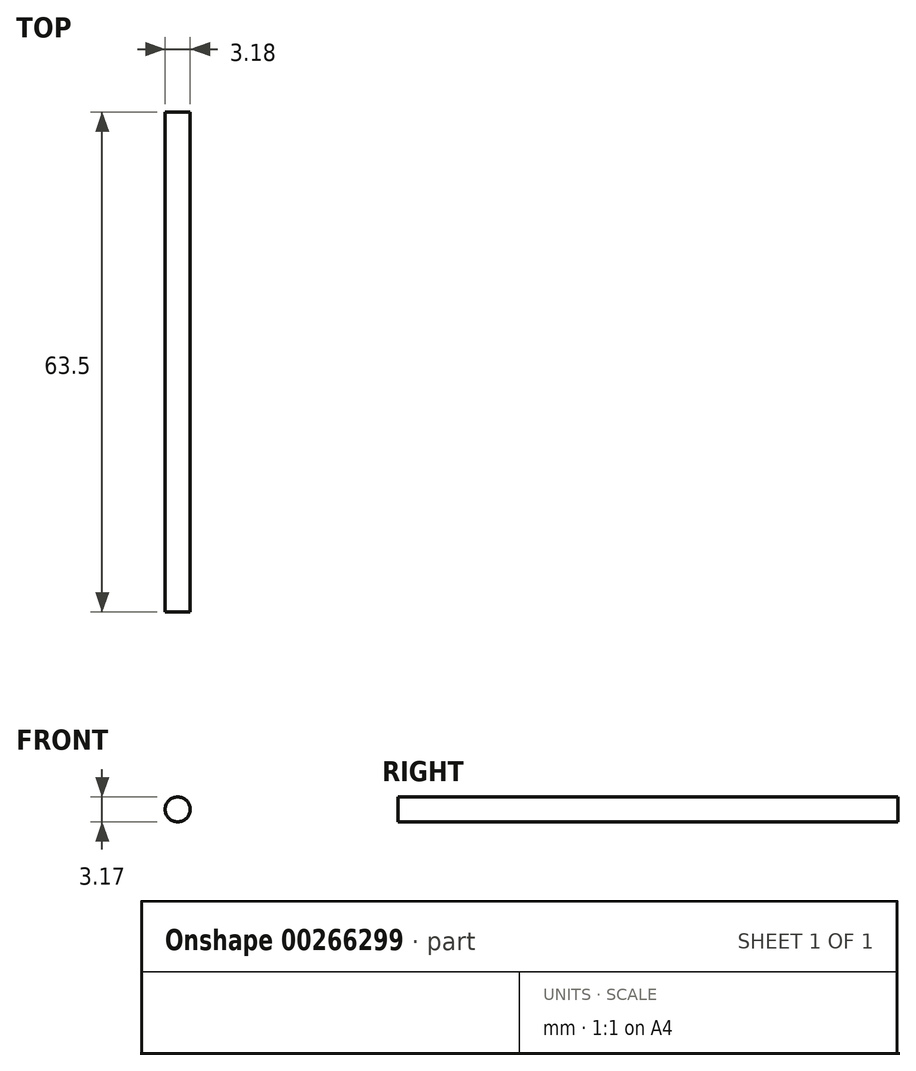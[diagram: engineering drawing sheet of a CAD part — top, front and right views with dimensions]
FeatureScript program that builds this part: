
annotation { "Feature Type Name" : "Feature", "Feature Type Description" : "" }
export const myFeature = defineFeature(function(context is Context, id is Id, definition is map)
    precondition{}
    {
        {
            var Q0;
            Q0=qCreatedBy(makeId("Front.planeOp"),FACE);
            var sketch = newSketch(context, id + "F0", { "sketchPlane" : qUnion([Q0])});
            skCircle(sketch, "E0", {"center": v(-39.23, 40.44) * mm, "radius": 1.59 * mm});
            skSolve(sketch);
        }
        {
            var Q0;
            Q0=makeQuery(id+"F0.imprint","IMPRINT",FACE,{"disambiguationData":[TD([[makeQuery(id+"F0.imprint","IMPRINT",EDGE,{"derivedFrom":sQuery(id+"F0.wireOp",EDGE,"E0")}),1.0]])]});
            extrude(context, id + "F1", {"entities" : qUnion([Q0]), "depth" : 63.5 * mm});
        }
    });
